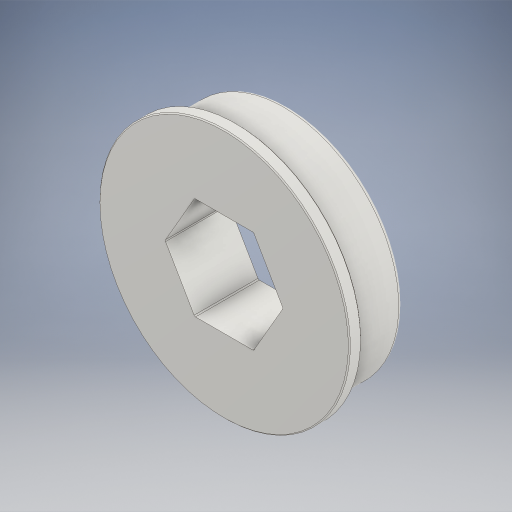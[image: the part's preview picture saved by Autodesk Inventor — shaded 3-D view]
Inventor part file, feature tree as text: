
AUTODESK INVENTOR PART (.ipt)
format: ipt  version: 2024.2 (Build 282272000, 272)  size: 329,216 bytes
history: native  units: in
note: dims shown in document units (in); Inventor stores cm internally (conversion verified against a paired STEP export)
features: fillet x1
ambient origin geometry x8: Origin, YZ Plane, XZ Plane, XY Plane, X Axis, Y Axis, Z Axis, Center Point
bodies: Solid1 (feature_tree)
feature tree (1):
  fillet  "Fillet2"  [1 undecoded]
note: 1 required parameter value undecoded (feature->parameter linkage not recoverable at this tier; creation-order binding heuristic only, values carry confidence <= 0.55)
